# Revit family: CLL
name_source: partatom
category: Lighting Fixtures
units: mm (PartAtom-declared; Revit-internal decimal feet)

## family parameters
Cut with Voids When Loaded = No
Host = Face
Light Source = Yes
OmniClass Number = 23.80.70.11
OmniClass Title = Luminaries for Internal Lighting
Part Type = Normal
Room Calculation Point = No
Round Connector Dimension = Use Diameter
Shared = No

## types (1)
- CLL
    Apparent Load = 10 VA
    Assembly Code = D5020200
    Color Filter = 16777215
    Default Elevation = 48 "
    Description = Compact concealed LED recessed self-contained emergency light with fully automatic operation suitable for wall or ceiling mount applications.
    Dimming Lamp Color Temperature Shift = <None>
    Features = Designed specifically for low level applications at 18" above floor level
Includes Self-Test, Self-Diagnostics with optional 15 min. time delay
6500K color temperature
LED life cycle of 10,000 hours
Dual-voltage field selectable 120 or 277VAC input
Rated for 2-hour runtime with Sealed Lead Acit or Nickel Cadmium batteries
Brownout Protection
Optional Remote Test Transmitter for ease of testing
    Housing = Paint  - White
    Lamp = LED Lamp
    Load Classification = Lighting
    Manufacturer = Dual Lite
    Material Finish = Green
    Model = CLL
    Opal lens = White Glass
    Photometric Note = For more Photometrics Please vist above Link
    Photometric Web File = CLL Low Level.ies
    Power Factor = 1
    Tilt Angle = -90.00°
    URL = https://www.currentlighting.com
    Voltage = 120 V
    Warranty = 3 year warranty
    Wattage Comments = 10W
    Watts = 10 W
    zz Length 1 = 23.7 "
    zz Length 2 = 23.7 "

## geometry (parser evidence)
native form markers: Sweep x1
no freeform markers — native parametric forms only
